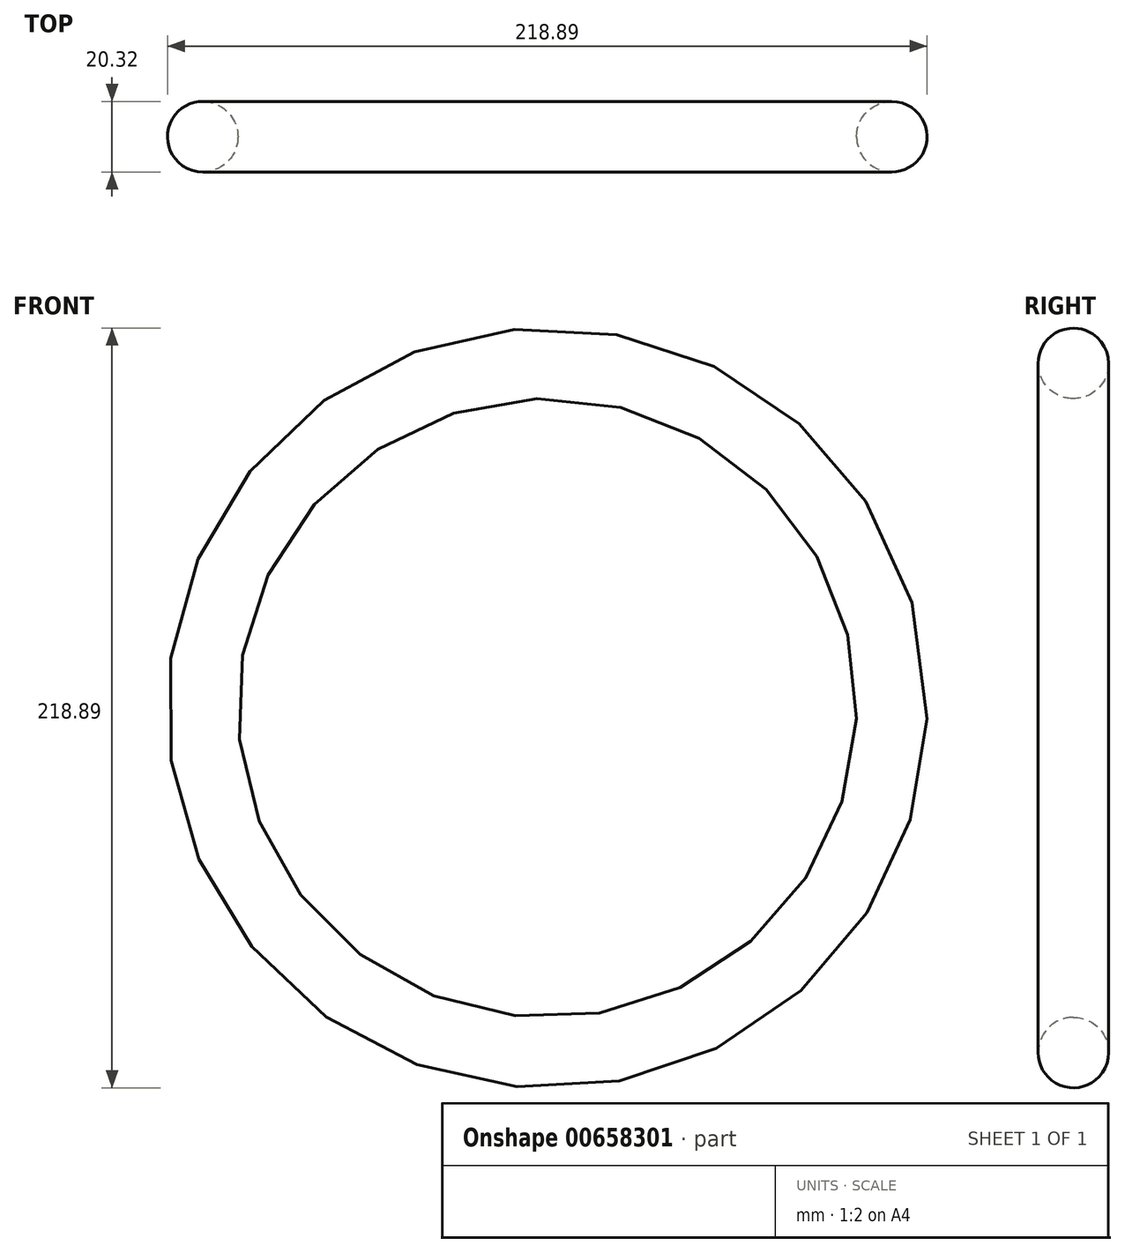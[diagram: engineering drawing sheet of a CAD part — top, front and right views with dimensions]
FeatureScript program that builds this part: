
annotation { "Feature Type Name" : "Feature", "Feature Type Description" : "" }
export const myFeature = defineFeature(function(context is Context, id is Id, definition is map)
    precondition{}
    {
        {
            var Q0;
            Q0=qCreatedBy(makeId("Top.planeOp"),FACE);
            var sketch = newSketch(context, id + "F0", { "sketchPlane" : qUnion([Q0])});
            skCircle(sketch, "E0", {"center": v(99.06, 0) * mm, "radius": 10.16 * mm});
            skCircle(sketch, "E1", {"center": v(-99.06, 0) * mm, "radius": 10.16 * mm});
            skPoint(sketch, "E2.center.orphan", {"position": v(0, 99.06) * mm});
            skPoint(sketch, "E3.center.orphan", {"position": v(0, -99.06) * mm});
            skSolve(sketch);
        }
        {
            var Q0;
            Q0=qCreatedBy(makeId("Front.planeOp"),FACE);
            var sketch = newSketch(context, id + "F1", { "sketchPlane" : qUnion([Q0])});
            skCircle(sketch, "E4", {"center": v(0.18, -3.07) * mm, "radius": 99.6 * mm});
            skPoint(sketch, "E4.first.point", {"position": v(-99.38, 0) * mm});
            skPoint(sketch, "E4.second.point", {"position": v(99.74, 0) * mm});
            skPoint(sketch, "E4.third.point", {"position": v(60.76, 76) * mm});
            skSolve(sketch);
        }
        {
            var Q0;
            Q0=makeQuery(id+"F0.imprint","IMPRINT",FACE,{"disambiguationData":[TD([[makeQuery(id+"F0.imprint","IMPRINT",EDGE,{"derivedFrom":sQuery(id+"F0.wireOp",EDGE,"E1")}),1.0]])]});
            var Q1;
            Q1=sQuery(id+"F1.wireOp",EDGE,"E4");
            sweep(context, id + "F2", {"profiles" : qUnion([Q0]), "path" : qUnion([Q1])});
        }
    });
